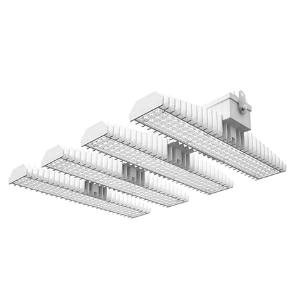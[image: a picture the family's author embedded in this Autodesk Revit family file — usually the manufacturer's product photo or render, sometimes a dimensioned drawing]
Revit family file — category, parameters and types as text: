
# Revit family: 3f_filippi_-_3f_lem_concentrato_3f_filippi_-_58908_a0811_-_3f_lem_4_led_200_dali_cr_conc___vt_63e8
name_source: partatom
category: Lighting Fixtures
units: mm (PartAtom-declared; Revit-internal decimal feet)

## family parameters
Cut with Voids When Loaded = No
Host = Face
Light Source = No
Part Type = Normal
Room Calculation Point = No
Round Connector Dimension = Use Diameter
Shared = No

## types (1)
- 3F Filippi - 3F LEM Concentrato (1 x LED, 30311 lm, 218 W, 4000 K)
    Apparent Load = 218 VA
    Approval mark = CE
    CIE Flux Codes = 83 96 99 100 100
    Color Rendering = 80
    Color Temperature = 4000 K
    Control Gear = Electronic transformer
    Default Elevation = 1800 mm
    Description = Industrial luminaire with high light output and high luminous efficiency designed with the most innovative technologies for environments with temperature up to 55°C.

ILLUMINOTECHNICAL
Luminous efficiency 100% (DLOR 99%, ULOR 1%).
Initial luminous flux of the luminaire 30311 lm.
Direct symmetric narrow distribution: the illuminated area has a elliptical shape.
Installation Interdistance Transv.D = 0.52 x hu - Long.D = 1.16 x hu.
Tabular UGR (CIE 117 - 4H-8H; S=0.25H; 70/50/20): RUG 17.2 - 21.
Beam angle: 31° - 73°.
Luminous efficacy 139 lm/W.
Lifetime (L93/B10): 30000 h. (tq+25°C)
Lifetime (L90/B10): 50000 h. (tq+25°C)
Lifetime (L85/B10): 80000 h. (tq+25°C)
Lifetime (L80/B10): 100000 h. (tq+25°C)
Lifetime (L85/B10): 50000 h. (tq+55°C)
Sudden decreased luminous flux after 50000 hours: 0% (C0).
Photobiological safety in compliance with IEC/TR 62778: RG0 risk exempt, (IEC 62471).
In compliance with IEC/EN 62722-2-1 - IEC/EN 62717 standards.

SOURCE
4 Mid-Power linear LED modules 50W/840.
Energy efficiency class (UE 2019/2020 - UE 2019/2015): C.
CIE 13.3 Colour rendering index: CRI >80 (R9 <50%).
IES TM-30 Fidelity Index: Rf = 84 Rg = 95.
CCT nominal colour temperature 4000 K.
Colour initial tolerance (MacAdam): SDCM 3.

MECHANICAL
Passive modular heatsinks in die-casted aluminium, painted in white colour.
To optimize the thermal management of the LED module, the heatsinks are oversized and provided with self-cleaning of cooling fins.
Wiring body in aluminium and galvanised steel anchored solidly to the sinks and thermally separated.
3F Lens lenses with high luminous efficiency, transparent methacrylate (PMMA), fixed to the LED modules.
Fixing brackets in stainless steel.
Luminaire with limited surface temperature. - D - (EN 60598-2-24)
Dimensions: 757x542 mm, height 133 mm. Weight 18.688 kg.
IP65 protection degree.
Mechanical strength to impacts IK06 (1 joule).
Glow-wire test resistance 650°C.

ELECTRICAL
Halogen Free DALI-2 DATI (Parts 251, 252, 253), PUSH-DIM, electronic wiring 230V-50/60Hz, power factor 0.97 at full load, THD <25%, constant output current, class I, 2 driver, 2 DALI addresses.
Power of the luminaire 218 W.
ENEC - CE.
Flicker: <4%.
Luminaire compliant with EN 60598-2-22 for power supply from a centralised emergency system CPSS (Central Power Supply System), not incorporated in the luminaire - high risk areas excluded. The default power and flux are 100% in AC and 15% in DC.
Ambient temperature from -30°C to +55°C.
Temperature class T6 max 85°C.
Quick connection via M25 5P connector with 9-13 mm tightening range.
Power unit positioned on a separate compartment by the LED module to ensure optimum temperatures of cabling components, to be inspectable and maintainable.
Relative humidity UR: <85%.

INSTALLATION
Ceiling / Suspended / Wall.
All accessories dedicated to this product are available on the Catalog and on our website www.3F-Filippi.com.

ACCESSORIES
A0811 - VT transparent glass, tempered, not flammable, with sealing gasket.
One required for each light module. The pack contains 10 pieces.

APPLICATIONS
In commercial environments, exhibition and industrial areas, stores, open areas or with shelves.
Applications with high ambient temperature up to 55°C.
Environments in which it is necessary a total protection against falling fragments (eg environments with foodstuffs or machines with moving parts or with extreme temperature changes), use luminaires with polycarbonate lenses.

LIGHT MANAGEMENT
Recommended minimum setting: 10%.
The luminaire, equipped with (DALI-2 DATI) driver, can be controlled manually with 3F Easy Dim technology or automatically/manually with wired or wireless DALI/D2D control systems.
The D2D driver guarantees interoperability with other devices with the same certification by making the following information available:
Device Data (Part 251), Energy Report (Part 252), Diagnosis & Maintenance (Part 253).
In electrical systems without a regulation system (manual or automatic) and DALI bus, a suitable jumper must be made on the DA-DA terminals of the appliance.

WARNING
Fixture not suitable for cold stores with an ambient temperature <0°C and/or relative humidity >85%.
Luminaire designed for disposal/recycling at end-of-life.
Replaceable (LED only) light source by a professional. Replaceable control gear by a professional.
    Height = 133 mm  [stored 0.436352 ft]
    Lamp = 1 x LED
    Lamp Light Flux = 30311 lm
    Lamp Power = 218 W
    Lamp count = 1
    Length = 757 mm
    Lifetime = 50000 h
    Luminous efficacy = 139 lm/W
    Manufacturer = 3F Filippi
    ModVariant = No
    Model = 3F Filippi - 58908+A0811 - 3F LEM 4 LED 200 DALI CR CONC + VT
    Mounting Place = Ceiling
    Mounting Type = Pendant
    Number of Poles = 1
    OnlyDefault = Yes
    Power Factor = 1
    Product Name = 3F Filippi - 3F LEM Concentrato
    Product group = pendant luminaire
    ProductGroupID = 9
    Protection Class = Protection class I
    Protection Degree = IP 65
    RLX_Detail_Level = 1
    RLX_Emergency_Light_Flux = 0 lm
    RLX_Emergency_Type = 0
    RLX_Emergency_Type_DB = No
    RlxData = <blob elided: 120649 chars, md5=1495ccdd>
    Socket = socket
    Standby Power = 0 W
    System Light Flux = 30311 lm
    System Power = 218 W
    Type Comments = Product without accessories
    Type Image = 3f_filippi_-_lem_4__a0811.jpg
    URL = http://relux.com
    VarID = ---
    Voltage = 0 V
    Weight = 0.00 kg
    Width = 542 mm

note: [stored X ft] marks values corroborated as IEEE doubles in the binary element streams (Revit-internal decimal feet)

## geometry (parser evidence)
native form markers: Blend x4, Sweep x13
no freeform markers — native parametric forms only
